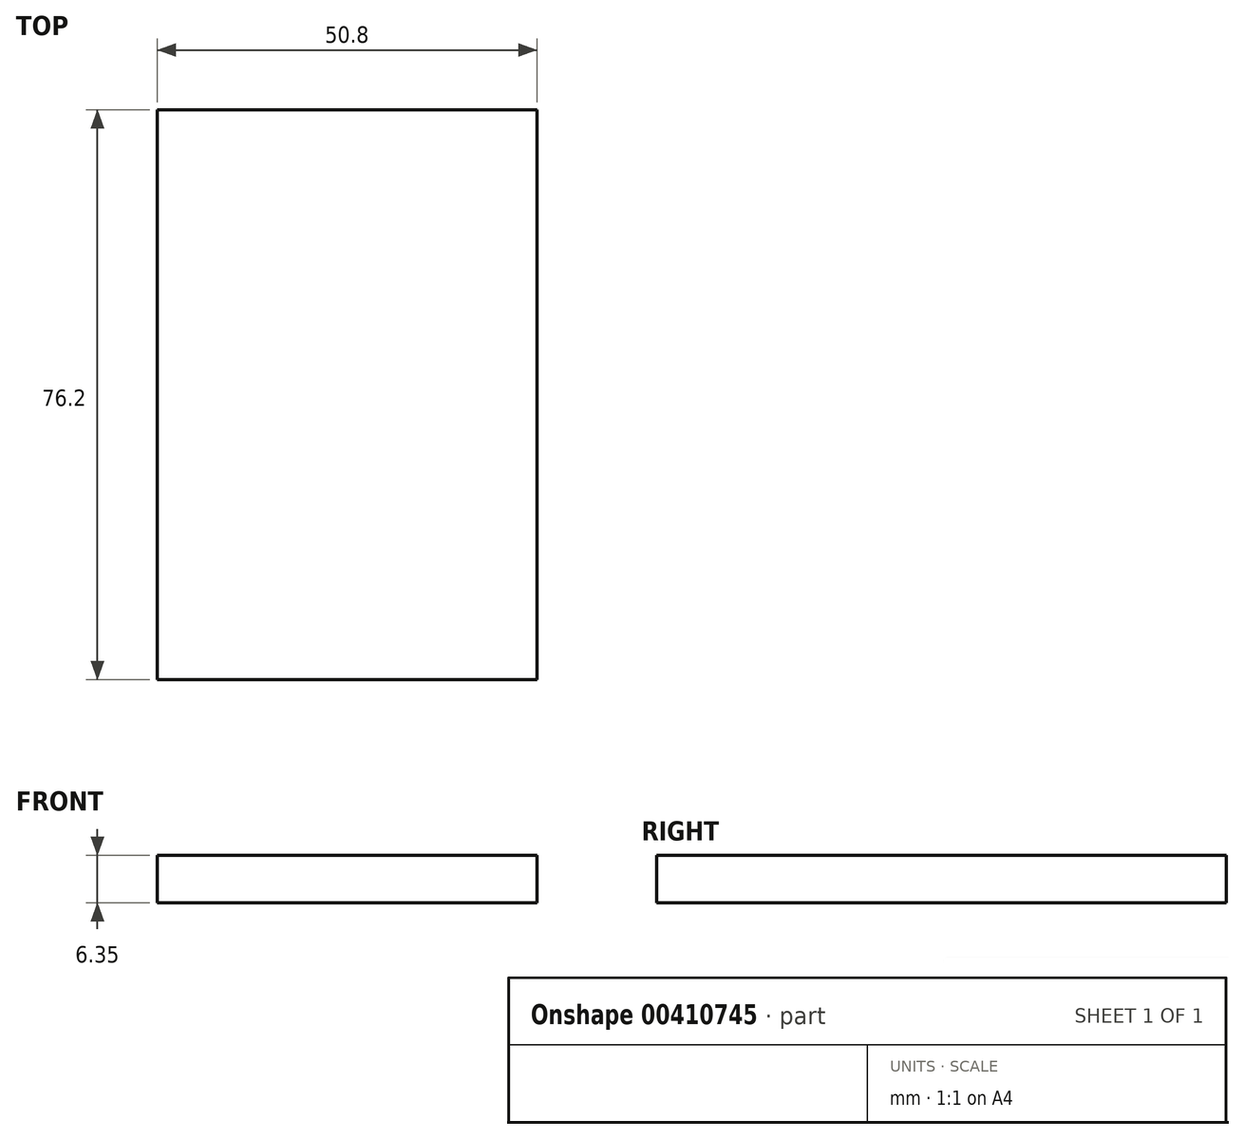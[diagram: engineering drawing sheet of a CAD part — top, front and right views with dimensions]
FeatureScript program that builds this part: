
annotation { "Feature Type Name" : "Feature", "Feature Type Description" : "" }
export const myFeature = defineFeature(function(context is Context, id is Id, definition is map)
    precondition{}
    {
        {
            var Q0;
            Q0=qCreatedBy(makeId("Top.planeOp"),FACE);
            var sketch = newSketch(context, id + "F0", { "sketchPlane" : qUnion([Q0])});
            skLineSegment(sketch, "E0.bottom", {"start": v(-29.54, -33.73) * mm, "end": v(21.26, -33.73) * mm});
            skLineSegment(sketch, "E0.top", {"start": v(-29.54, 42.47) * mm, "end": v(21.26, 42.47) * mm});
            skLineSegment(sketch, "E0.left", {"start": v(-29.54, -33.73) * mm, "end": v(-29.54, 42.47) * mm});
            skLineSegment(sketch, "E0.right", {"start": v(21.26, -33.73) * mm, "end": v(21.26, 42.47) * mm});
            skSolve(sketch);
        }
        {
            var Q0;
            Q0=sQuery(id+"F0.wireOp",EDGE,"E0.right");
            var Q1;
            Q1=sQuery(id+"F0.wireOp",EDGE,"E0.left");
            var Q2;
            Q2=sQuery(id+"F0.wireOp",EDGE,"E0.top");
            var Q3;
            Q3=sQuery(id+"F0.wireOp",EDGE,"E0.bottom");
            extrude(context, id + "F1", {"bodyType" : ToolBodyType.SURFACE, "surfaceEntities" : qUnion([Q0, Q1, Q2, Q3]), "depth" : 6.35 * mm});
        }
    });
